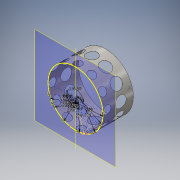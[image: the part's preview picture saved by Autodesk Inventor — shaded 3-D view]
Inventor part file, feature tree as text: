
AUTODESK INVENTOR PART (.ipt)
format: ipt  version: 2016 (Build 200138000, 138)  size: 1,694,208 bytes
history: native  units: mm
features: sketch x12, other x11, plane x8, sheet_metal_op x3, projected_geometry x3
ambient origin geometry x8: Origin, YZ Plane, XZ Plane, XY Plane, X Axis, Y Axis, Z Axis, Center Point
bodies: Body1 (feature_tree)
feature tree (37):
  sketch  "Sketch1"  dims[d0=3.0mm]
  sketch  "3D Sketch1"
  sheet_metal_op  "Contour Flange2"
  sketch  "Sketch5"  dims[d18=1.0mm]
  plane  "Work Plane1"
  plane  "Work Plane2"
  plane  "Work Plane3"
  plane  "Work Plane4"
  plane  "Work Plane5"
  plane  "Work Plane6"
  plane  "Work Plane7"
  plane  "Work Plane8"
  other  "Helical Curve1"
  sketch  "Sketch3"  dims[d1=1.2mm d2=10.18mm d3=457.2mm]
  other  "Plate2"
  sheet_metal_op  "Bend2"
  sheet_metal_op  "Corner2"
  sketch  "Sketch6"  dims[d19=0.5mm]
  sketch  "Sketch7"  dims[d20=2.0mm]
  sketch  "Sketch8"  dims[d21=1.0mm]
  sketch  "Sketch9"  dims[d22=254.0mm]
  sketch  "Sketch10"  dims[d23=1.0mm]
  sketch  "Sketch11"  dims[d24=1.0mm]
  projected_geometry  "Projected Loop1"
  projected_geometry  "Projected Loop2"
  projected_geometry  "Projected Loop3"
  sketch  "Sketch12"  dims[d25=4.0mm]
  sketch  "Sketch13"  dims[d26=1.0mm d27=1.0mm d34=229.0mm d35=21.554816mm d36=64.0mm d37=91.0mm d38=35.5mm d39=150.0mm d40=1.0mm d41=0.0mm d42=229.0mm d43=16.318829mm d44=64.0mm d45=91.0mm d46=35.5mm d47=150.0mm d48=1.0mm d49=0.0mm d50=229.0mm d51=26.790804mm d52=229.0mm d53=32.026792mm d54=229.0mm d55=11.082841mm d56=229.0mm d57=5.846853mm d58=64.0mm d59=91.0mm d60=35.5mm d61=150.0mm d62=1.0mm d63=0.0mm d64=64.0mm d65=91.0mm d66=35.5mm d67=150.0mm d68=1.0mm d69=0.0mm d70=64.0mm d71=91.0mm d72=35.5mm d73=150.0mm d74=1.0mm d75=0.0mm d76=64.0mm d77=91.0mm d78=35.5mm d79=150.0mm d80=1.0mm d81=0.0mm d82=5.0mm d83=5.0mm d84=5.0mm d85=5.0mm d86=5.0mm d87=25.0mm d88=51.0mm d89=127.0mm d90=178.0mm d91=229.0mm d92=8.0mm d93=0.0mm d94=229.0mm d95=3.228859mm d96=12.0mm d97=229.0mm d98=50.0mm d99=1.0mm d100=0.0mm]
  other  "Cut2"
  other  "Cut3"
  other  "Cut4"
  other  "Cut5"
  other  "Cut6"
  other  "Cut7"
  other  "Cut8"
  other  "Cut9"
  other  "Definition1"
